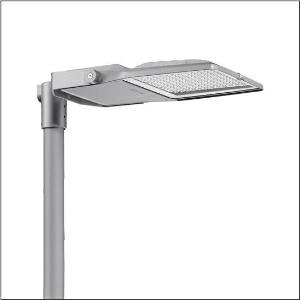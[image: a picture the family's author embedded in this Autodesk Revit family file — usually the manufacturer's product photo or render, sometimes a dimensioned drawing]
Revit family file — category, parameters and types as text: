
# Revit family: floodlight_fl_21_iq_midi___pl52_5xa7781f2d3a_fab9
name_source: partatom
category: Lighting Fixtures
units: mm (PartAtom-declared; Revit-internal decimal feet)

## family parameters
Cut with Voids When Loaded = No
Host = Face
Light Source = No
Part Type = Normal
Room Calculation Point = No
Round Connector Dimension = Use Diameter
Shared = No

## types (1)
- --- (1 x LED, 35760 lm, 270.2 W, 3000K)
    Apparent Load = 270 VA
    CIE Flux Codes = 26 60 98 100 100
    Color Rendering = 70
    Color Temperature = 3000K
    Default Elevation = 1800 mm
    Description = Floodlight FL 21 iQ midi, floodlight, primary light control with lens, of PMMA, primary optical cover: protective disc, of toughened safety glass, transparent, light distribution: PL52, light emission: direct distribution, installation type: surface-mounted, LED, High Power LED, rated luminous flux: 35.760lm, luminous efficacy: 132lm/W, light colour: 730, colour temperature: 3000K, control gear: ECG iQ, control: optimised constant luminous flux control (CLO 2.0), Desk-Remote (wireless, voltage-free reading and setting of iQ features in the workshop via application-optimized NFC function/RFID function), Light-Fading, Smart-Wire, Night-Set, Lumen-Switch, Temp-Guard, Auto-Match, with terminal, 6-pole, mains connection: 220..240V, AC, 50/60Hz, start of lifetime: 270W, end of service life: 287W, reduction: 117W, luminaire housing, of diecast aluminium, powder-coated, Siteco® metallic grey (DB 702S), corrosivity category C5 mid according to DIN EN ISO 12944, sealing non-destructively replaceable, please order mast flange separately, mast bracket, of steel, galvanised, powder-coated, Siteco® metallic grey (DB 702S), protection rating (complete): IP66, insulation class (complete): insulation class II (safety insulation), certification: CE, protection symbol: D, impact resistance: IK08, permissible operating ambient temperature: -40..+40°C, permissible operating ambient temperature for outdoor applications: -40..+50°C, standard: DIN EN 12944, LABS conformity tested according to VDMA 24364:2018-05, packaging unit: 1 piece

Light Distribution: PL52
    Height = 76 mm
    Lamp = 1 x LED
    Lamp Light Flux = 35760 lm
    Lamp Power = 270.2 W
    Lamp count = 1
    Length = 657 mm
    Luminous efficacy = 132 lm/W
    Manufacturer = Siteco
    ModVariant = No
    Model = 5XA7781F2D3A
    Number of Poles = 1
    OnlyDefault = Yes
    Power Factor = 1
    Product Name = Floodlight FL 21 iQ midi | PL52
    Product group = floodlight | pylon annexe
    ProductGroupID = 6200
    Protection Class = Protection class II
    Protection Degree = IP 66
    RLX_Detail_Level = 1
    RLX_Emergency_Light_Flux = 0 lm
    RLX_Emergency_Type = 0
    RLX_Emergency_Type_DB = No
    RlxData = <blob elided: 153613 chars, md5=c1e20710>
    Socket = socket
    Standby Power = 0 W
    System Light Flux = 35760 lm
    System Power = 270 W
    Type Comments = factory setting: luminous flux: 100 % | dim-lin: 254 | 620 mA
    Type Image = l_1007123.jpg
    URL = http://relux.com
    VarID = @adj_054111
    Voltage = 0 V
    Weight = 0.00 kg
    Width = 442 mm

## geometry (parser evidence)
native form markers: Blend x4, Sweep x12
no freeform markers — native parametric forms only
